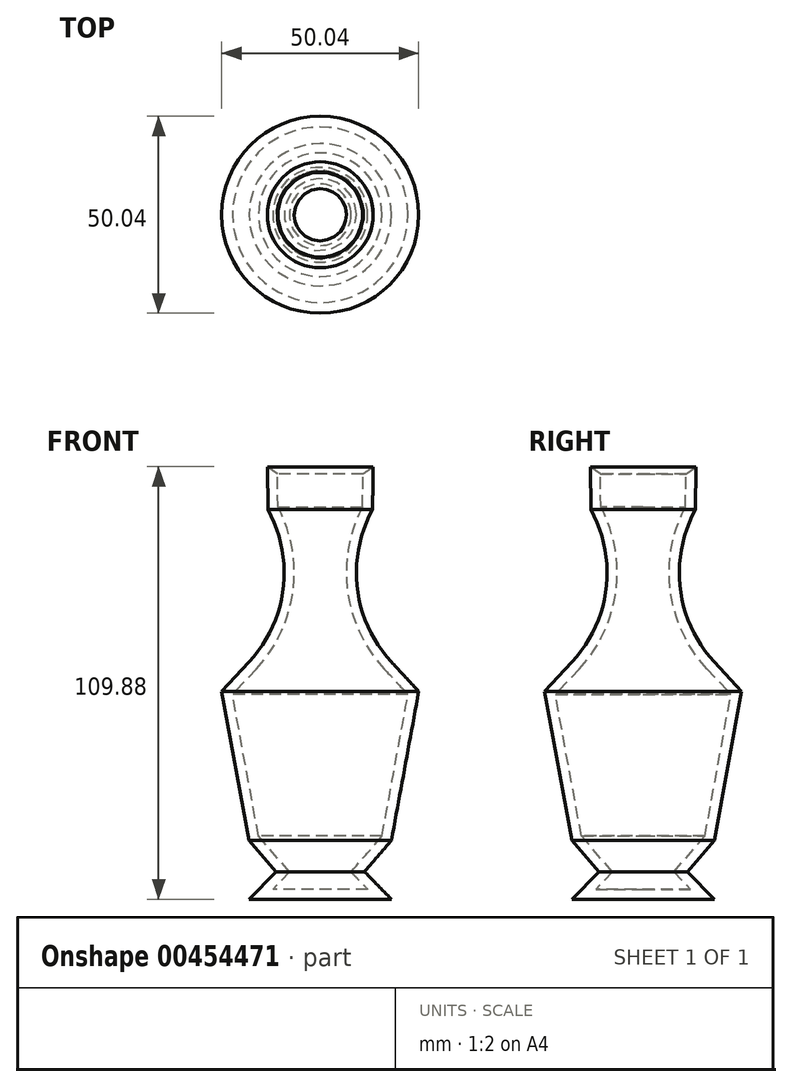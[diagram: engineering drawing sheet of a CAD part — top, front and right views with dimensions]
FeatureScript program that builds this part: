
annotation { "Feature Type Name" : "Feature", "Feature Type Description" : "" }
export const myFeature = defineFeature(function(context is Context, id is Id, definition is map)
    precondition{}
    {
        {
            var Q0;
            Q0=qCreatedBy(makeId("Front.planeOp"),FACE);
            var sketch = newSketch(context, id + "F0", { "sketchPlane" : qUnion([Q0])});
            skLineSegment(sketch, "E0", {"start": v(0, 46.27) * mm, "end": v(0, -54.2) * mm});
            skLineSegment(sketch, "E1", {"start": v(0, -54.2) * mm, "end": v(18.07, -54.2) * mm});
            skLineSegment(sketch, "E2", {"start": v(18.07, -54.2) * mm, "end": v(11.25, -47.2) * mm});
            skLineSegment(sketch, "E3", {"start": v(11.25, -47.2) * mm, "end": v(18.07, -39.3) * mm});
            skLineSegment(sketch, "E4", {"start": v(18.07, -39.3) * mm, "end": v(25.02, -1.4) * mm});
            skLineSegment(sketch, "E5", {"start": v(25.02, -1.4) * mm, "end": v(18.07, 6.08) * mm});
            skArc(sketch, "E6", {"start": v(18.07, 6.08) * mm, "mid": v(9.42, 24.67) * mm, "end": v(13.27, 44.8) * mm});
            skLineSegment(sketch, "E7", {"start": v(13.27, 44.8) * mm, "end": v(13.46, 55.68) * mm});
            skLineSegment(sketch, "E8", {"start": v(0, 46.27) * mm, "end": v(13.46, 55.68) * mm});
            skSolve(sketch);
        }
        {
            var Q0;
            Q0 = qSketchRegion(id + "F0", true);
            var Q1;
            {var subQ2=sQuery(id+"F0.wireOp",EDGE,"E0");Q1=makeQuery(id+"F0.imprint","IMPRINT",FACE,{"disambiguationData":[TD([[makeQuery(id+"F0.imprint","IMPRINT",EDGE,{"derivedFrom":subQ2}),1.0]])]});}
            var Q2;
            Q2=sQuery(id+"F0.wireOp",EDGE,"E0");
            revolve(context, id + "F1", {"entities" : qUnion([Q0, Q1]), "axis" : qUnion([Q2]), "revolveType" : RevolveType.FULL});
        }
        {
            var Q0;
            Q0=makeQuery(id+"F1.opRevolve","SWEPT_FACE",FACE,{"disambiguationData":[OSD([sQuery(id+"F0.wireOp",EDGE,"E8")])]});
            shell(context, id + "F2", {"entities" : qUnion([Q0]), "thickness" : 2.54 * mm});
        }
    });
